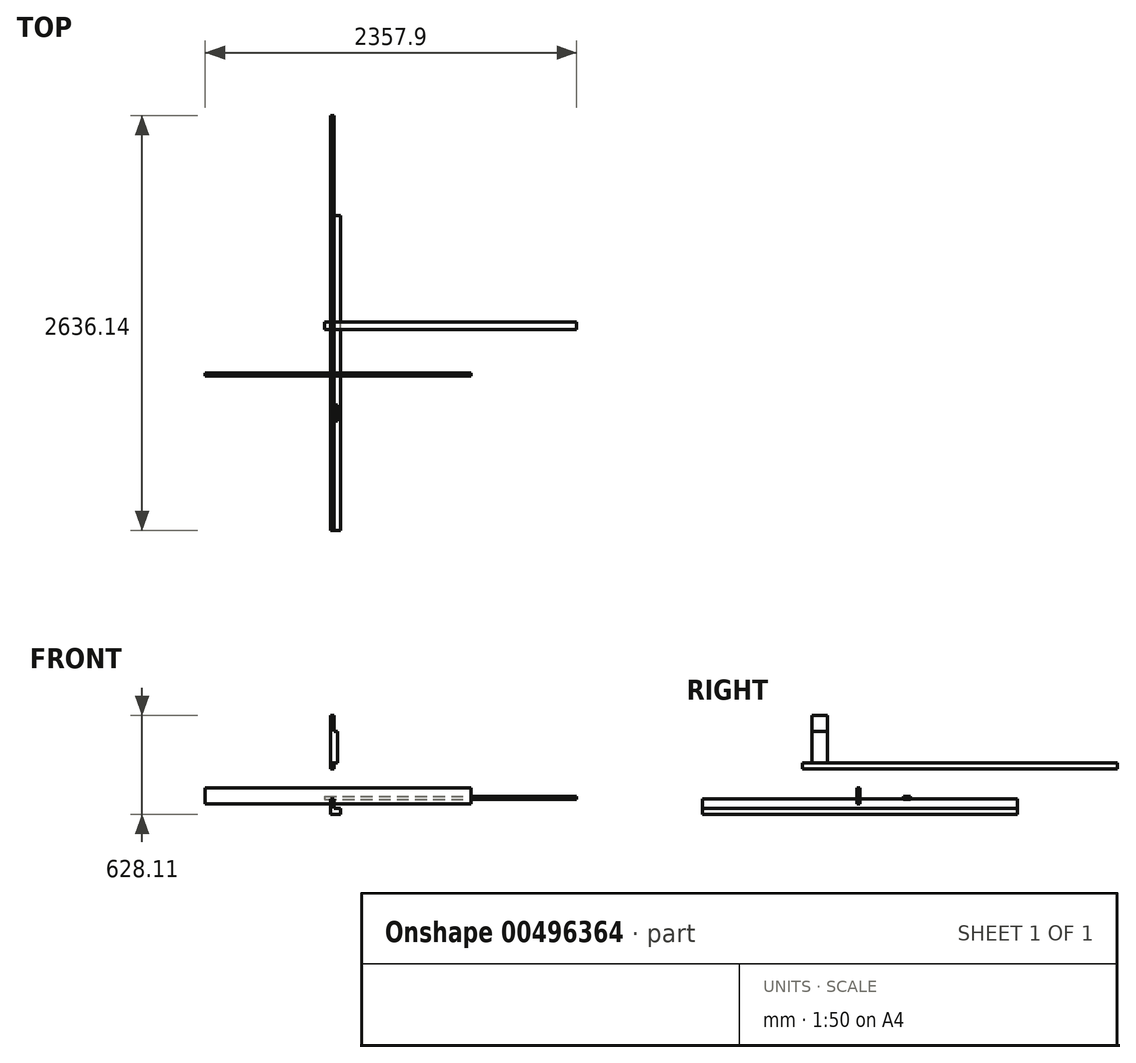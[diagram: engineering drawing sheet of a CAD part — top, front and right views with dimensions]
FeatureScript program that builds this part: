
annotation { "Feature Type Name" : "Feature", "Feature Type Description" : "" }
export const myFeature = defineFeature(function(context is Context, id is Id, definition is map)
    precondition{}
    {
        {
            assignVariable(context, id + "F0", {"name" : "w", "anyValue" : 22});
        }
        {
            var Q0;
            Q0=qCreatedBy(makeId("Right.planeOp"),FACE);
            var sketch = newSketch(context, id + "F1", { "sketchPlane" : qUnion([Q0])});
            skLineSegment(sketch, "E0.bottom", {"start": v(-1001.96, 6.24) * mm, "end": v(998.04, 6.24) * mm});
            skLineSegment(sketch, "E0.top", {"start": v(-1001.96, -93.76) * mm, "end": v(998.04, -93.76) * mm});
            skLineSegment(sketch, "E0.left", {"start": v(-1001.96, 6.24) * mm, "end": v(-1001.96, -93.76) * mm});
            skLineSegment(sketch, "E0.right", {"start": v(998.04, 6.24) * mm, "end": v(998.04, -93.76) * mm});
            skLineSegment(sketch, "E1", {"start": v(-1001.96, -55.76) * mm, "end": v(998.04, -55.76) * mm});
            skSolve(sketch);
        }
        {
            var Q0;
            {var subQ0=sQuery(id+"F1.wireOp",EDGE,"E0.bottom");Q0=makeQuery(id+"F1.imprint","IMPRINT",FACE,{"disambiguationData":[TD([[makeQuery(id+"F1.imprint","IMPRINT",EDGE,{"derivedFrom":subQ0}),-1.0]])]});}
            extrude(context, id + "F2", {"entities" : qUnion([Q0]), "depth" : (getVariable(context, 'w')) * mm});
        }
        {
            var Q0;
            {var subQ0=sQuery(id+"F1.wireOp",EDGE,"E0.top");Q0=makeQuery(id+"F1.imprint","IMPRINT",FACE,{"disambiguationData":[TD([[makeQuery(id+"F1.imprint","IMPRINT",EDGE,{"derivedFrom":subQ0}),1.0]])]});}
            extrude(context, id + "F3", {"entities" : qUnion([Q0]), "operationType" : NewBodyOperationType.ADD, "depth" : (getVariable(context, 'w') + 40) * mm});
        }
        {
            var Q0;
            Q0=qCreatedBy(makeId("Front.planeOp"),FACE);
            var sketch = newSketch(context, id + "F4", { "sketchPlane" : qUnion([Q0])});
            skLineSegment(sketch, "E2.bottom", {"start": v(-796.18, 73.07) * mm, "end": v(891.82, 73.07) * mm});
            skLineSegment(sketch, "E2.top", {"start": v(-796.18, -26.93) * mm, "end": v(891.82, -26.93) * mm});
            skLineSegment(sketch, "E2.left", {"start": v(-796.18, 73.07) * mm, "end": v(-796.18, -26.93) * mm});
            skLineSegment(sketch, "E2.right", {"start": v(891.82, 73.07) * mm, "end": v(891.82, -26.93) * mm});
            skSolve(sketch);
        }
        {
            var Q0;
            Q0=makeQuery(id+"F4.imprint","IMPRINT",FACE,{"disambiguationData":[TD([[makeQuery(id+"F4.imprint","IMPRINT",EDGE,{"derivedFrom":sQuery(id+"F4.wireOp",EDGE,"E2.bottom")}),-1.0]])]});
            extrude(context, id + "F5", {"entities" : qUnion([Q0]), "depth" : (getVariable(context, 'w')) * mm});
        }
        {
            var Q0;
            Q0=qCreatedBy(makeId("Right.planeOp"),FACE);
            var sketch = newSketch(context, id + "F6", { "sketchPlane" : qUnion([Q0])});
            skLineSegment(sketch, "E3.bottom", {"start": v(-365.82, 234.43) * mm, "end": v(1634.18, 234.43) * mm});
            skLineSegment(sketch, "E3.top", {"start": v(-365.82, 196.43) * mm, "end": v(1634.18, 196.43) * mm});
            skLineSegment(sketch, "E3.left", {"start": v(-365.82, 234.43) * mm, "end": v(-365.82, 196.43) * mm});
            skLineSegment(sketch, "E3.right", {"start": v(1634.18, 234.43) * mm, "end": v(1634.18, 196.43) * mm});
            skSolve(sketch);
        }
        {
            var Q0;
            Q0=makeQuery(id+"F6.imprint","IMPRINT",FACE,{"disambiguationData":[TD([[makeQuery(id+"F6.imprint","IMPRINT",EDGE,{"derivedFrom":sQuery(id+"F6.wireOp",EDGE,"E3.bottom")}),-1.0]])]});
            extrude(context, id + "F7", {"entities" : qUnion([Q0]), "depth" : (getVariable(context, 'w')) * mm});
        }
        {
            var Q0;
            Q0=qCreatedBy(makeId("Top.planeOp"),FACE);
            var sketch = newSketch(context, id + "F8", { "sketchPlane" : qUnion([Q0])});
            skLineSegment(sketch, "E4.bottom", {"start": v(-38.28, 320.98) * mm, "end": v(1561.72, 320.98) * mm});
            skLineSegment(sketch, "E4.top", {"start": v(-38.28, 275.98) * mm, "end": v(1561.72, 275.98) * mm});
            skLineSegment(sketch, "E4.left", {"start": v(-38.28, 320.98) * mm, "end": v(-38.28, 275.98) * mm});
            skLineSegment(sketch, "E4.right", {"start": v(1561.72, 320.98) * mm, "end": v(1561.72, 275.98) * mm});
            skSolve(sketch);
        }
        {
            var Q0;
            Q0=makeQuery(id+"F8.imprint","IMPRINT",FACE,{"disambiguationData":[TD([[makeQuery(id+"F8.imprint","IMPRINT",EDGE,{"derivedFrom":sQuery(id+"F8.wireOp",EDGE,"E4.bottom")}),-1.0]])]});
            extrude(context, id + "F9", {"entities" : qUnion([Q0]), "depth" : (getVariable(context, 'w')) * mm});
        }
        {
            var Q0;
            Q0=qCreatedBy(makeId("Right.planeOp"),FACE);
            var sketch = newSketch(context, id + "F10", { "sketchPlane" : qUnion([Q0])});
            skLineSegment(sketch, "E5.bottom", {"start": v(-306.3, 534.35) * mm, "end": v(-206.3, 534.35) * mm});
            skLineSegment(sketch, "E5.top", {"start": v(-306.3, 234.35) * mm, "end": v(-206.3, 234.35) * mm});
            skLineSegment(sketch, "E5.left", {"start": v(-306.3, 534.35) * mm, "end": v(-306.3, 234.35) * mm});
            skLineSegment(sketch, "E5.right", {"start": v(-206.3, 534.35) * mm, "end": v(-206.3, 234.35) * mm});
            skLineSegment(sketch, "E6", {"start": v(-306.3, 434.35) * mm, "end": v(-206.3, 434.35) * mm});
            skSolve(sketch);
        }
        {
            var Q0;
            {var subQ0=sQuery(id+"F10.wireOp",EDGE,"E5.bottom");Q0=makeQuery(id+"F10.imprint","IMPRINT",FACE,{"disambiguationData":[TD([[makeQuery(id+"F10.imprint","IMPRINT",EDGE,{"derivedFrom":subQ0}),-1.0]])]});}
            extrude(context, id + "F11", {"entities" : qUnion([Q0]), "depth" : (getVariable(context, 'w')) * mm});
        }
        {
            var Q0;
            {var subQ0=sQuery(id+"F10.wireOp",EDGE,"E5.top");Q0=makeQuery(id+"F10.imprint","IMPRINT",FACE,{"disambiguationData":[TD([[makeQuery(id+"F10.imprint","IMPRINT",EDGE,{"derivedFrom":subQ0}),1.0]])]});}
            extrude(context, id + "F12", {"entities" : qUnion([Q0]), "operationType" : NewBodyOperationType.ADD, "depth" : (getVariable(context, 'w') * 2) * mm});
        }
    });
